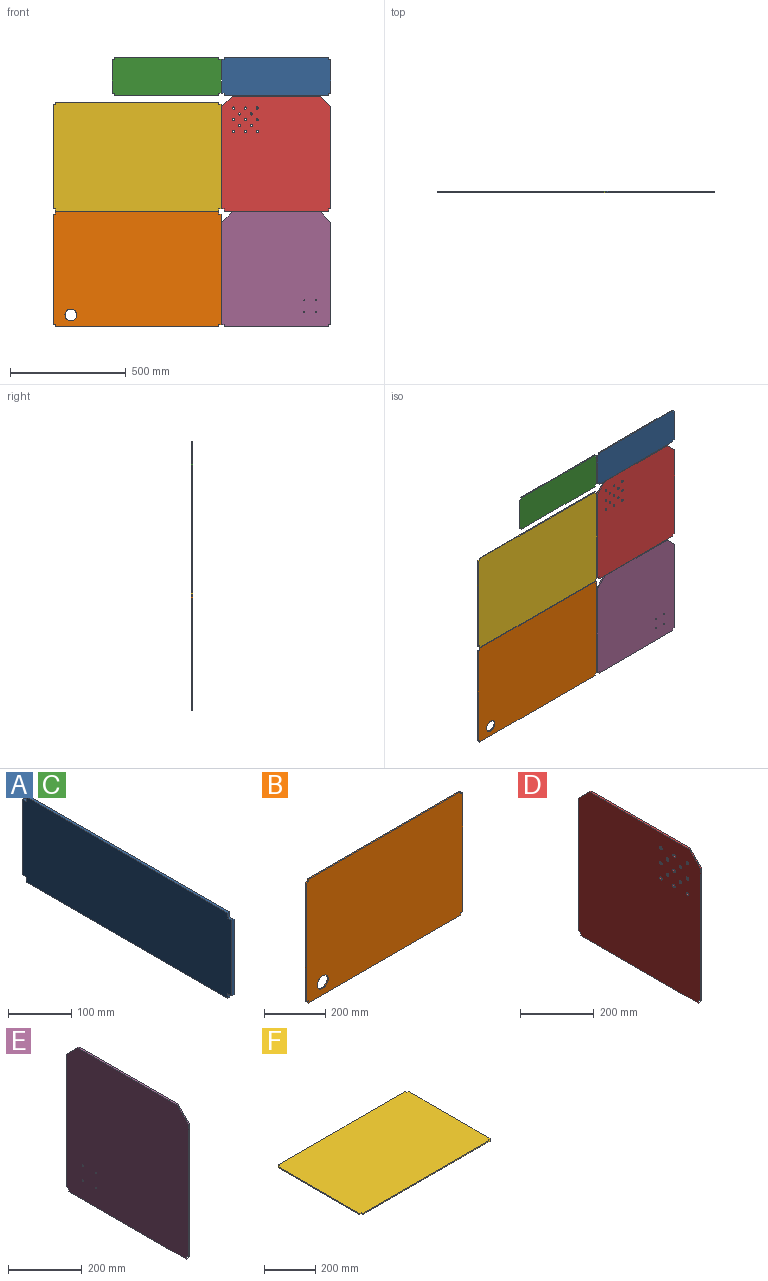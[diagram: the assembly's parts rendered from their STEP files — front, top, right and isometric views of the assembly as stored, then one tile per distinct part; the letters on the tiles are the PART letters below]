
ASSEMBLY  parts=6 mates=5
PART A: 14 faces, bbox 4.8x469.9x165.1 mm
  f0: plane 146.05x4.76mm, normal (0,-1,0), area 695.6mm2, adj f1,f11,f12,f13
  f1: plane 9.53x4.76mm, normal (0,0,-1), area 45.4mm2, adj f0,f2,f12,f13
  f2: plane 9.53x4.76mm, normal (0,-1,0), area 45.4mm2, adj f1,f3,f12,f13
  f3: plane 450.85x4.76mm, normal (0,0,-1), area 2147.2mm2, adj f2,f4,f12,f13
  f4: plane 9.53x4.76mm, normal (0,1,0), area 45.4mm2, adj f3,f5,f12,f13
  f5: plane 9.53x4.76mm, normal (0,0,-1), area 45.4mm2, adj f4,f6,f12,f13
  f6: plane 146.05x4.76mm, normal (0,1,0), area 695.6mm2, adj f5,f7,f12,f13
  f7: plane 9.53x4.76mm, normal (0,0,1), area 45.4mm2, adj f6,f8,f12,f13
  f8: plane 9.53x4.76mm, normal (0,1,0), area 45.4mm2, adj f7,f9,f12,f13
  f9: plane 450.85x4.76mm, normal (0,0,1), area 2147.2mm2, adj f8,f10,f12,f13
  f10: plane 9.53x4.76mm, normal (0,-1,0), area 45.4mm2, adj f9,f11,f12,f13
  f11: plane 9.53x4.76mm, normal (0,0,1), area 45.4mm2, adj f0,f10,f12,f13
  f12: plane 469.9x165.1mm, normal (1,0,0), area 77217.6mm2, adj f0,f1,f2,f3,f4,f5,f6,f7
  f13: plane 469.9x165.1mm, normal (-1,0,0), area 77217.6mm2, adj f0,f1,f2,f3,f4,f5,f6,f7
PART B: 15 faces, bbox 723.9x4.8x495.3 mm
  f0: plane 704.85x4.76mm, normal (0,0,1), area 3356.8mm2, adj f1,f12,f13,f14
  f1: plane 9.53x4.76mm, normal (-1,0,0), area 45.4mm2, adj f0,f2,f13,f14
  f2: plane 9.53x4.76mm, normal (0,0,1), area 45.4mm2, adj f1,f3,f13,f14
  f3: plane 476.25x4.76mm, normal (-1,0,0), area 2268.1mm2, adj f2,f4,f13,f14
  f4: plane 9.53x4.76mm, normal (0,0,-1), area 45.4mm2, adj f3,f5,f13,f14
  f5: plane 9.53x4.76mm, normal (-1,0,0), area 45.4mm2, adj f4,f6,f13,f14
  f6: plane 704.85x4.76mm, normal (0,0,-1), area 3356.8mm2, adj f5,f7,f13,f14
  f7: plane 9.53x4.76mm, normal (1,0,0), area 45.4mm2, adj f6,f8,f13,f14
  f8: plane 9.53x4.76mm, normal (0,0,-1), area 45.4mm2, adj f7,f9,f13,f14
  f9: plane 476.25x4.76mm, normal (1,0,0), area 2268.1mm2, adj f8,f10,f13,f14
  f10: plane 9.53x4.76mm, normal (0,0,1), area 45.4mm2, adj f9,f12,f13,f14
  f11: cylinder r=25.4mm len=50.8mm, axis (0,1,0), area 760.1mm2, adj f13,f14
  f12: plane 9.53x4.76mm, normal (1,0,0), area 45.4mm2, adj f0,f10,f13,f14
  f13: plane 723.9x495.3mm, normal (0,-1,0), area 356157.9mm2, adj f0,f1,f2,f3,f4,f5,f6,f7
  f14: plane 723.9x495.3mm, normal (0,1,0), area 356157.9mm2, adj f0,f1,f2,f3,f4,f5,f6,f7
PART C: same geometry as A
PART D: 25 faces, bbox 4.8x469.9x495.3 mm
  f0: plane 44.45x44.45mm, normal (0,-0.71,0.71), area 299.4mm2, adj f1,f21,f23,f24
  f1: plane 441.33x4.76mm, normal (0,-1,0), area 2101.8mm2, adj f0,f2,f23,f24
  f2: plane 9.53x4.76mm, normal (0,0,-1), area 45.4mm2, adj f1,f3,f23,f24
  f3: plane 9.53x4.76mm, normal (0,-1,0), area 45.4mm2, adj f2,f4,f23,f24
  f4: plane 450.85x4.76mm, normal (0,0,-1), area 2147.2mm2, adj f3,f5,f23,f24
  f5: plane 9.53x4.76mm, normal (0,1,0), area 45.4mm2, adj f4,f6,f23,f24
  f6: plane 9.53x4.76mm, normal (0,0,-1), area 45.4mm2, adj f5,f7,f23,f24
  f7: plane 441.33x4.76mm, normal (0,1,0), area 2101.8mm2, adj f6,f8,f23,f24
  f8: plane 44.45x44.45mm, normal (0,0.71,0.71), area 299.4mm2, adj f7,f21,f23,f24
  f9: cylinder r=4.76mm len=9.53mm, axis (-1,0,0), area 142.5mm2, adj f23,f24
  f10: cylinder r=4.76mm len=9.53mm, axis (-1,0,0), area 142.5mm2, adj f23,f24
  f11: cylinder r=4.76mm len=9.53mm, axis (-1,0,0), area 142.5mm2, adj f23,f24
  f12: cylinder r=4.76mm len=9.53mm, axis (-1,0,0), area 142.5mm2, adj f23,f24
  f13: cylinder r=4.76mm len=9.53mm, axis (-1,0,0), area 142.5mm2, adj f23,f24
  f14: cylinder r=4.76mm len=9.53mm, axis (-1,0,0), area 142.5mm2, adj f23,f24
  f15: cylinder r=4.76mm len=9.53mm, axis (-1,0,0), area 142.5mm2, adj f23,f24
  f16: cylinder r=4.76mm len=9.53mm, axis (-1,0,0), area 142.5mm2, adj f23,f24
  f17: cylinder r=4.76mm len=9.53mm, axis (-1,0,0), area 142.5mm2, adj f23,f24
  f18: cylinder r=4.76mm len=9.53mm, axis (-1,0,0), area 142.5mm2, adj f23,f24
  f19: cylinder r=4.76mm len=9.53mm, axis (-1,0,0), area 142.5mm2, adj f23,f24
  f20: cylinder r=4.76mm len=9.53mm, axis (-1,0,0), area 142.5mm2, adj f23,f24
  f21: plane 381x4.76mm, normal (0,0,1), area 1814.5mm2, adj f0,f8,f23,f24
  f22: cylinder r=4.76mm len=9.53mm, axis (-1,0,0), area 142.5mm2, adj f23,f24
  f23: plane 495.3x469.9mm, normal (1,0,0), area 229657.9mm2, adj f0,f1,f2,f3,f4,f5,f6,f7
  f24: plane 495.3x469.9mm, normal (-1,0,0), area 229657.9mm2, adj f0,f1,f2,f3,f4,f5,f6,f7
PART E: 16 faces, bbox 4.8x469.9x495.3 mm
  f0: plane 44.45x44.45mm, normal (0,-0.71,0.71), area 299.4mm2, adj f1,f9,f10,f11
  f1: plane 441.33x4.76mm, normal (0,-1,0), area 2101.8mm2, adj f0,f2,f10,f11
  f2: plane 9.53x4.76mm, normal (0,0,-1), area 45.4mm2, adj f1,f3,f10,f11
  f3: plane 9.53x4.76mm, normal (0,-1,0), area 45.4mm2, adj f2,f4,f10,f11
  f4: plane 450.85x4.76mm, normal (0,0,-1), area 2147.2mm2, adj f3,f5,f10,f11
  f5: plane 9.53x4.76mm, normal (0,1,0), area 45.4mm2, adj f4,f6,f10,f11
  f6: plane 9.53x4.76mm, normal (0,0,-1), area 45.4mm2, adj f5,f7,f10,f11
  f7: plane 441.33x4.76mm, normal (0,1,0), area 2101.8mm2, adj f6,f8,f10,f11
  f8: plane 44.45x44.45mm, normal (0,0.71,0.71), area 299.4mm2, adj f7,f9,f10,f11
  f9: plane 381x4.76mm, normal (0,0,1), area 1814.5mm2, adj f0,f8,f10,f11
  f10: plane 495.3x469.9mm, normal (1,0,0), area 230525.6mm2, adj f0,f1,f2,f3,f4,f5,f6,f7
  f11: plane 495.3x469.9mm, normal (-1,0,0), area 230525.6mm2, adj f0,f1,f2,f3,f4,f5,f6,f7
  f12: cylinder r=2.16mm len=4.76mm, axis (-1,0,0), area 64.6mm2, adj f10,f11
  f13: cylinder r=2.16mm len=4.76mm, axis (-1,0,0), area 64.6mm2, adj f10,f11
  f14: cylinder r=2.16mm len=4.76mm, axis (-1,0,0), area 64.6mm2, adj f10,f11
  f15: cylinder r=2.16mm len=4.76mm, axis (-1,0,0), area 64.6mm2, adj f10,f11
PART F: 14 faces, bbox 723.9x469.9x4.8 mm
  f0: plane 450.85x4.76mm, normal (-1,0,0), area 2147.2mm2, adj f1,f11,f12,f13
  f1: plane 9.53x4.76mm, normal (0,-1,0), area 45.4mm2, adj f0,f2,f12,f13
  f2: plane 9.53x4.76mm, normal (-1,0,0), area 45.4mm2, adj f1,f3,f12,f13
  f3: plane 704.85x4.76mm, normal (0,-1,0), area 3356.8mm2, adj f2,f4,f12,f13
  f4: plane 9.53x4.76mm, normal (1,0,0), area 45.4mm2, adj f3,f5,f12,f13
  f5: plane 9.53x4.76mm, normal (0,-1,0), area 45.4mm2, adj f4,f6,f12,f13
  f6: plane 450.85x4.76mm, normal (1,0,0), area 2147.2mm2, adj f5,f7,f12,f13
  f7: plane 9.53x4.76mm, normal (0,1,0), area 45.4mm2, adj f6,f8,f12,f13
  f8: plane 9.53x4.76mm, normal (1,0,0), area 45.4mm2, adj f7,f9,f12,f13
  f9: plane 704.85x4.76mm, normal (0,1,0), area 3356.8mm2, adj f8,f10,f12,f13
  f10: plane 9.53x4.76mm, normal (-1,0,0), area 45.4mm2, adj f9,f11,f12,f13
  f11: plane 9.53x4.76mm, normal (0,1,0), area 45.4mm2, adj f0,f10,f12,f13
  f12: plane 723.9x469.9mm, normal (0,0,1), area 339797.7mm2, adj f0,f1,f2,f3,f4,f5,f6,f7
  f13: plane 723.9x469.9mm, normal (0,0,-1), area 339797.7mm2, adj f0,f1,f2,f3,f4,f5,f6,f7
PLACE A rot(axis=(0,0,-1),90deg) t=(365.12,4.76,1006.48)mm
PLACE B t=(0,4.76,247.65)mm
PLACE C rot(axis=(0,0,-1),90deg) t=(-107.95,4.76,1006.48)mm
PLACE D rot(axis=(0,0,-1),90deg) t=(600.08,4.76,746.13)mm
PLACE E rot(axis=(0,0,-1),90deg) t=(600.08,4.76,247.65)mm
PLACE F rot(axis=(-1,0,0),90deg) t=(0,0,733.42)mm
MATE fastened D.f23 <-> A.f12  axis (0,-1,0) through (600.07,0,993.78)mm
MATE fastened B.f13 <-> E.f10  axis (0,-1,0) through (361.95,0,9.53)mm
MATE fastened A.f12 <-> C.f12  axis (0,-1,0) through (365.12,0,1006.48)mm
MATE fastened F.f10 <-> B.f1  axis (-1,0,0) through (-352.42,2.38,498.48)mm
MATE fastened D.f23 <-> E.f10  axis (0,-1,0) through (600.08,0,498.47)mm
